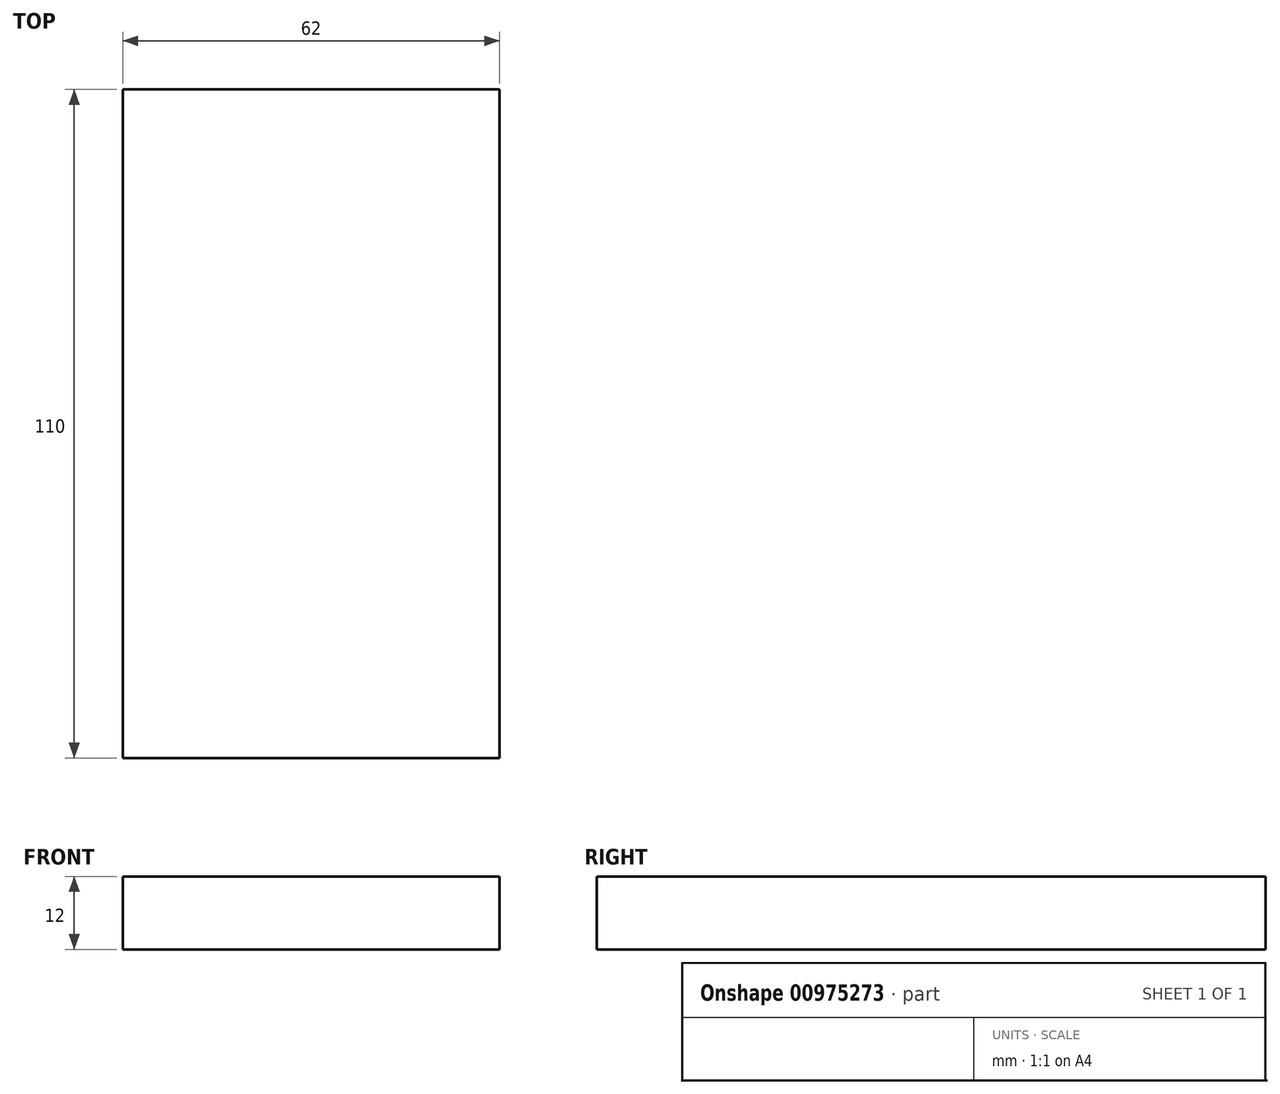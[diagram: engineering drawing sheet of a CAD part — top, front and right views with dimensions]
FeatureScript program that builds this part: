
annotation { "Feature Type Name" : "Feature", "Feature Type Description" : "" }
export const myFeature = defineFeature(function(context is Context, id is Id, definition is map)
    precondition{}
    {
        {
            var Q0;
            Q0=qCreatedBy(makeId("Top.planeOp"),FACE);
            var sketch = newSketch(context, id + "F0", { "sketchPlane" : qUnion([Q0])});
            skLineSegment(sketch, "E0.bottom", {"start": v(31, 55) * mm, "end": v(-31, 55) * mm});
            skLineSegment(sketch, "E0.top", {"start": v(31, -55) * mm, "end": v(-31, -55) * mm});
            skLineSegment(sketch, "E0.left", {"start": v(31, 55) * mm, "end": v(31, -55) * mm});
            skLineSegment(sketch, "E0.right", {"start": v(-31, 55) * mm, "end": v(-31, -55) * mm});
            skPoint(sketch, "E0.middle", {"position": v(0, 0) * mm});
            skSolve(sketch);
        }
        {
            var Q0;
            Q0=makeQuery(id+"F0.imprint","IMPRINT",FACE,{"disambiguationData":[TD([[makeQuery(id+"F0.imprint","IMPRINT",EDGE,{"derivedFrom":sQuery(id+"F0.wireOp",EDGE,"E0.bottom")}),1.0]])]});
            extrude(context, id + "F1", {"entities" : qUnion([Q0]), "depth" : 12 * mm, "offsetDistance" : 25 * mm});
        }
    });
